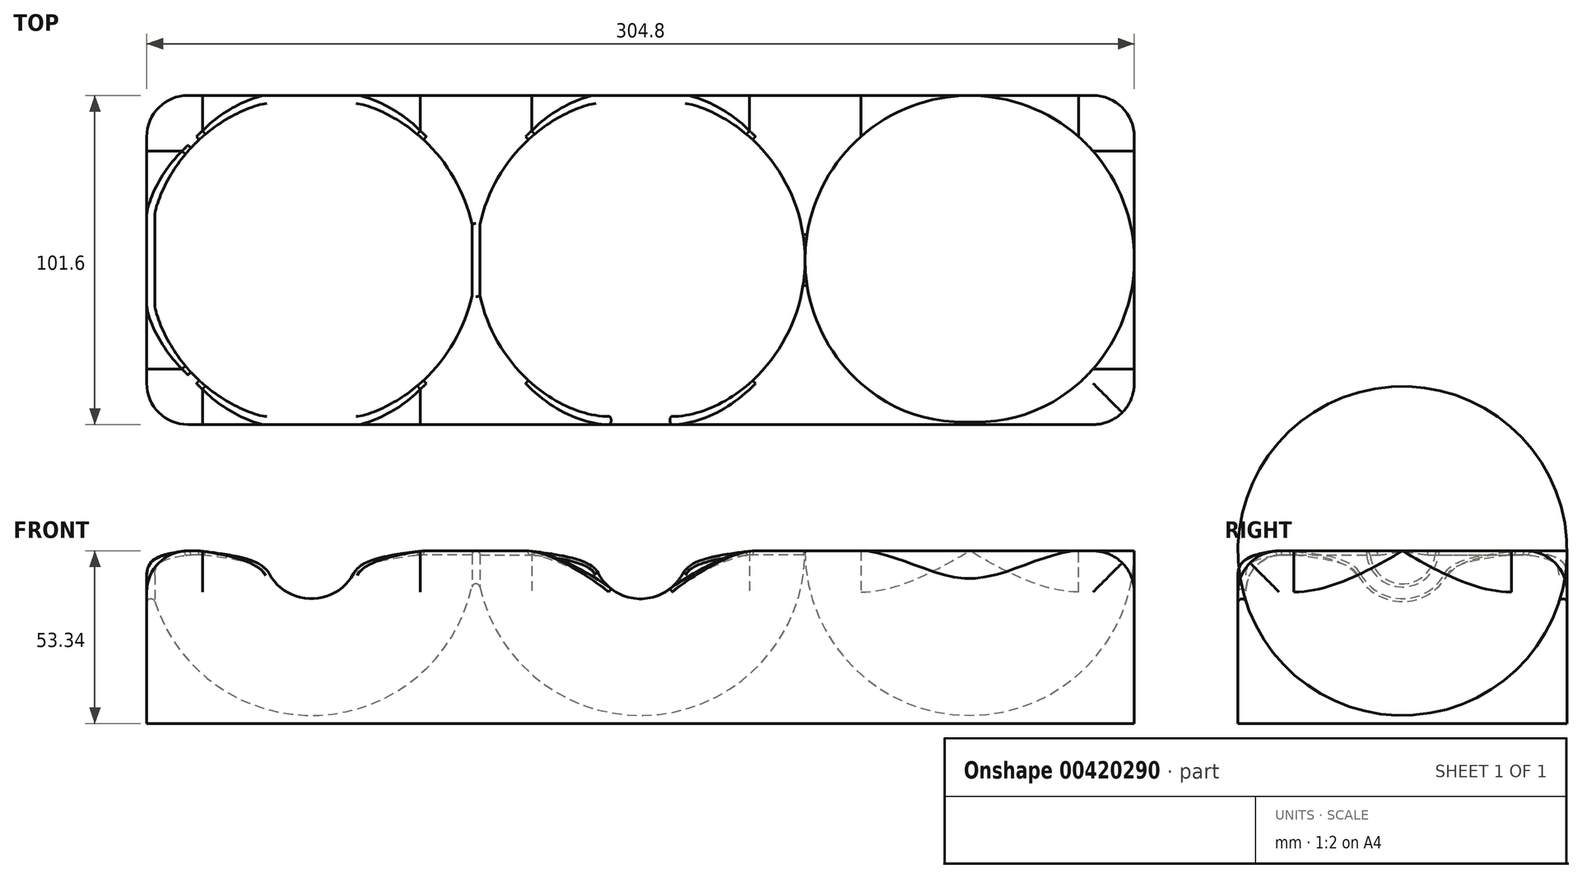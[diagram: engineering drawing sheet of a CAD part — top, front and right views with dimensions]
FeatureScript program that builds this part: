
annotation { "Feature Type Name" : "Feature", "Feature Type Description" : "" }
export const myFeature = defineFeature(function(context is Context, id is Id, definition is map)
    precondition{}
    {
        {
            var Q0;
            Q0=qCreatedBy(makeId("Top.planeOp"),FACE);
            var sketch = newSketch(context, id + "F0", { "sketchPlane" : qUnion([Q0])});
            skLineSegment(sketch, "E0.bottom", {"start": v(-140.38, -23.85) * mm, "end": v(164.42, -23.85) * mm});
            skLineSegment(sketch, "E0.top", {"start": v(-140.38, -125.45) * mm, "end": v(164.42, -125.45) * mm});
            skLineSegment(sketch, "E0.left", {"start": v(-140.38, -23.85) * mm, "end": v(-140.38, -125.45) * mm});
            skLineSegment(sketch, "E0.right", {"start": v(164.42, -23.85) * mm, "end": v(164.42, -125.45) * mm});
            skSolve(sketch);
        }
        {
            var Q0;
            Q0=makeQuery(id+"F0.imprint","IMPRINT",FACE,{"disambiguationData":[TD([[makeQuery(id+"F0.imprint","IMPRINT",EDGE,{"derivedFrom":sQuery(id+"F0.wireOp",EDGE,"E0.bottom")}),-1.0]])]});
            extrude(context, id + "F1", {"entities" : qUnion([Q0]), "depth" : 53.34 * mm});
        }
        {
            var Q0;
            Q0=makeQuery(id+"F1.opExtrude","CAP_FACE",FACE,{"disambiguationData":[OSD([sQuery(id+"F0.wireOp",EDGE,"E0.bottom"),sQuery(id+"F0.wireOp",EDGE,"E0.top"),sQuery(id+"F0.wireOp",EDGE,"E0.left"),sQuery(id+"F0.wireOp",EDGE,"E0.right")])],"isStart":false});
            var sketch = newSketch(context, id + "F2", { "sketchPlane" : qUnion([Q0])});
            skLineSegment(sketch, "E1", {"start": v(-140.38, -23.85) * mm, "end": v(-89.58, -23.85) * mm});
            skLineSegment(sketch, "E2", {"start": v(-89.58, -23.85) * mm, "end": v(-89.58, -125.45) * mm});
            skArc(sketch, "E3", {"start": v(-89.58, -23.85) * mm, "mid": v(-140.38, -74.65) * mm, "end": v(-89.58, -125.45) * mm});
            skArc(sketch, "E4.1.0.0", {"start": v(12.02, -23.85) * mm, "mid": v(-38.78, -74.65) * mm, "end": v(12.02, -125.45) * mm});
            skLineSegment(sketch, "E4.1.0.1", {"start": v(12.02, -23.85) * mm, "end": v(12.02, -125.45) * mm});
            skArc(sketch, "E4.2.0.0", {"start": v(113.62, -23.85) * mm, "mid": v(62.82, -74.65) * mm, "end": v(113.62, -125.45) * mm});
            skLineSegment(sketch, "E4.2.0.1", {"start": v(113.62, -23.85) * mm, "end": v(113.62, -125.45) * mm});
            skLineSegment(sketch, "E4.direction1", {"start": v(-89.58, -125.45) * mm, "end": v(12.02, -125.45) * mm, "construction": true});
            skSolve(sketch);
        }
        {
            var Q0;
            {var subQ0=sQuery(id+"F2.wireOp",EDGE,"E2");Q0=makeQuery(id+"F2.imprint","IMPRINT",FACE,{"disambiguationData":[TD([[makeQuery(id+"F2.imprint","IMPRINT",EDGE,{"derivedFrom":subQ0}),-1.0]])]});}
            var Q1;
            Q1=sQuery(id+"F2.wireOp",EDGE,"E2");
            revolve(context, id + "F3", {"operationType" : NewBodyOperationType.REMOVE, "entities" : qUnion([Q0]), "axis" : qUnion([Q1]), "revolveType" : RevolveType.FULL, "oppositeDirection" : true});
        }
        {
            var Q0;
            Q0=makeQuery(id+"F2.imprint","IMPRINT",FACE,{"disambiguationData":[TD([[makeQuery(id+"F2.imprint","IMPRINT",EDGE,{"derivedFrom":sQuery(id+"F2.wireOp",EDGE,"E4.1.0.0")}),1.0]])]});
            var Q1;
            Q1=sQuery(id+"F2.wireOp",EDGE,"E4.1.0.1");
            revolve(context, id + "F4", {"operationType" : NewBodyOperationType.REMOVE, "entities" : qUnion([Q0]), "axis" : qUnion([Q1]), "revolveType" : RevolveType.FULL, "oppositeDirection" : true});
        }
        {
            var Q0;
            Q0=makeQuery(id+"F2.imprint","IMPRINT",FACE,{"disambiguationData":[TD([[makeQuery(id+"F2.imprint","IMPRINT",EDGE,{"derivedFrom":sQuery(id+"F2.wireOp",EDGE,"E4.2.0.0")}),1.0]])]});
            var Q1;
            Q1=sQuery(id+"F2.wireOp",EDGE,"E4.2.0.1");
            revolve(context, id + "F5", {"operationType" : NewBodyOperationType.REMOVE, "entities" : qUnion([Q0]), "axis" : qUnion([Q1]), "revolveType" : RevolveType.FULL, "oppositeDirection" : true});
        }
        {
            var Q0;
            {var subQ0=sQuery(id+"F0.wireOp",EDGE,"E0.right");var subQ1=sQuery(id+"F0.wireOp",EDGE,"E0.top");var subQ4=makeQuery(id+"F3.opRevolve","SWEPT_FACE",FACE,{"disambiguationData":[OSD([sQuery(id+"F2.wireOp",EDGE,"E3")])]});Q0=makeQuery(id+"F4.boolean.opBoolean","SPLIT",EDGE,{"disambiguationData":[TD([makeQuery(id+"F3.boolean.opBoolean","COPY",FACE,{"derivedFrom":subQ4})])],"derivedFrom":makeQuery(id+"F3.boolean.opBoolean","SPLIT",EDGE,{"disambiguationData":[TD([makeQuery(id+"F1.opExtrude","SWEPT_FACE",FACE,{"disambiguationData":[OSD([subQ0])]})])],"derivedFrom":makeQuery(id+"F1.opExtrude","CAP_EDGE",EDGE,{"disambiguationData":[OSD([subQ1])],"isStart":false})})});}
            var Q1;
            {var subQ0=sQuery(id+"F0.wireOp",EDGE,"E0.left");var subQ1=sQuery(id+"F0.wireOp",EDGE,"E0.top");Q1=makeQuery(id+"F3.boolean.opBoolean","SPLIT",EDGE,{"disambiguationData":[TD([makeQuery(id+"F1.opExtrude","SWEPT_FACE",FACE,{"disambiguationData":[OSD([subQ0])]})])],"derivedFrom":makeQuery(id+"F1.opExtrude","CAP_EDGE",EDGE,{"disambiguationData":[OSD([subQ1])],"isStart":false})});}
            var Q2;
            {var subQ0=sQuery(id+"F0.wireOp",EDGE,"E0.left");var subQ1=sQuery(id+"F0.wireOp",EDGE,"E0.top");Q2=makeQuery(id+"F3.boolean.opBoolean","SPLIT",EDGE,{"disambiguationData":[TD([makeQuery(id+"F1.opExtrude","SWEPT_FACE",FACE,{"disambiguationData":[OSD([subQ1])]})])],"derivedFrom":makeQuery(id+"F1.opExtrude","CAP_EDGE",EDGE,{"disambiguationData":[OSD([subQ0])],"isStart":false})});}
            var Q3;
            {var subQ0=sQuery(id+"F0.wireOp",EDGE,"E0.bottom");var subQ1=sQuery(id+"F0.wireOp",EDGE,"E0.left");Q3=makeQuery(id+"F3.boolean.opBoolean","SPLIT",EDGE,{"disambiguationData":[TD([makeQuery(id+"F1.opExtrude","SWEPT_FACE",FACE,{"disambiguationData":[OSD([subQ0])]})])],"derivedFrom":makeQuery(id+"F1.opExtrude","CAP_EDGE",EDGE,{"disambiguationData":[OSD([subQ1])],"isStart":false})});}
            var Q4;
            {var subQ0=sQuery(id+"F0.wireOp",EDGE,"E0.bottom");var subQ1=sQuery(id+"F0.wireOp",EDGE,"E0.left");Q4=makeQuery(id+"F3.boolean.opBoolean","SPLIT",EDGE,{"disambiguationData":[TD([makeQuery(id+"F1.opExtrude","SWEPT_FACE",FACE,{"disambiguationData":[OSD([subQ1])]})])],"derivedFrom":makeQuery(id+"F1.opExtrude","CAP_EDGE",EDGE,{"disambiguationData":[OSD([subQ0])],"isStart":false})});}
            var Q5;
            {var subQ0=sQuery(id+"F0.wireOp",EDGE,"E0.bottom");var subQ2=sQuery(id+"F0.wireOp",EDGE,"E0.right");var subQ4=makeQuery(id+"F3.opRevolve","SWEPT_FACE",FACE,{"disambiguationData":[OSD([sQuery(id+"F2.wireOp",EDGE,"E3")])]});Q5=makeQuery(id+"F4.boolean.opBoolean","SPLIT",EDGE,{"disambiguationData":[TD([makeQuery(id+"F3.boolean.opBoolean","COPY",FACE,{"derivedFrom":subQ4})])],"derivedFrom":makeQuery(id+"F3.boolean.opBoolean","SPLIT",EDGE,{"disambiguationData":[TD([makeQuery(id+"F1.opExtrude","SWEPT_FACE",FACE,{"disambiguationData":[OSD([subQ2])]})])],"derivedFrom":makeQuery(id+"F1.opExtrude","CAP_EDGE",EDGE,{"disambiguationData":[OSD([subQ0])],"isStart":false})})});}
            var Q6;
            {var subQ0=sQuery(id+"F0.wireOp",EDGE,"E0.bottom");var subQ2=sQuery(id+"F0.wireOp",EDGE,"E0.right");var subQ4=makeQuery(id+"F4.opRevolve","SWEPT_FACE",FACE,{"disambiguationData":[OSD([sQuery(id+"F2.wireOp",EDGE,"E4.1.0.0")])]});var subQ5=makeQuery(id+"F1.opExtrude","SWEPT_FACE",FACE,{"disambiguationData":[OSD([subQ2])]});Q6=makeQuery(id+"F5.boolean.opBoolean","SPLIT",EDGE,{"disambiguationData":[TD([makeQuery(id+"F4.boolean.opBoolean","COPY",FACE,{"derivedFrom":subQ4})])],"derivedFrom":makeQuery(id+"F4.boolean.opBoolean","SPLIT",EDGE,{"disambiguationData":[TD([subQ5])],"derivedFrom":makeQuery(id+"F3.boolean.opBoolean","SPLIT",EDGE,{"disambiguationData":[TD([subQ5])],"derivedFrom":makeQuery(id+"F1.opExtrude","CAP_EDGE",EDGE,{"disambiguationData":[OSD([subQ0])],"isStart":false})})})});}
            var Q7;
            {var subQ0=sQuery(id+"F0.wireOp",EDGE,"E0.bottom");var subQ2=sQuery(id+"F0.wireOp",EDGE,"E0.right");var subQ3=makeQuery(id+"F1.opExtrude","SWEPT_FACE",FACE,{"disambiguationData":[OSD([subQ2])]});Q7=makeQuery(id+"F5.boolean.opBoolean","SPLIT",EDGE,{"disambiguationData":[TD([subQ3])],"derivedFrom":makeQuery(id+"F4.boolean.opBoolean","SPLIT",EDGE,{"disambiguationData":[TD([subQ3])],"derivedFrom":makeQuery(id+"F3.boolean.opBoolean","SPLIT",EDGE,{"disambiguationData":[TD([subQ3])],"derivedFrom":makeQuery(id+"F1.opExtrude","CAP_EDGE",EDGE,{"disambiguationData":[OSD([subQ0])],"isStart":false})})})});}
            var Q8;
            {var subQ0=sQuery(id+"F0.wireOp",EDGE,"E0.bottom");var subQ1=sQuery(id+"F0.wireOp",EDGE,"E0.right");Q8=makeQuery(id+"F5.boolean.opBoolean","SPLIT",EDGE,{"disambiguationData":[TD([makeQuery(id+"F1.opExtrude","SWEPT_FACE",FACE,{"disambiguationData":[OSD([subQ0])]})])],"derivedFrom":makeQuery(id+"F1.opExtrude","CAP_EDGE",EDGE,{"disambiguationData":[OSD([subQ1])],"isStart":false})});}
            var Q9;
            {var subQ0=sQuery(id+"F0.wireOp",EDGE,"E0.right");var subQ1=sQuery(id+"F0.wireOp",EDGE,"E0.top");Q9=makeQuery(id+"F5.boolean.opBoolean","SPLIT",EDGE,{"disambiguationData":[TD([makeQuery(id+"F1.opExtrude","SWEPT_FACE",FACE,{"disambiguationData":[OSD([subQ1])]})])],"derivedFrom":makeQuery(id+"F1.opExtrude","CAP_EDGE",EDGE,{"disambiguationData":[OSD([subQ0])],"isStart":false})});}
            var Q10;
            Q10=makeQuery(id+"F1.opExtrude","SWEPT_EDGE",EDGE,{"disambiguationData":[OSD([sQuery(id+"F0.wireOp",EDGE,"E0.top"),sQuery(id+"F0.wireOp",EDGE,"E0.right")])]});
            var Q11;
            Q11=makeQuery(id+"F1.opExtrude","SWEPT_EDGE",EDGE,{"disambiguationData":[OSD([sQuery(id+"F0.wireOp",EDGE,"E0.bottom"),sQuery(id+"F0.wireOp",EDGE,"E0.right")])]});
            var Q12;
            Q12=makeQuery(id+"F1.opExtrude","SWEPT_EDGE",EDGE,{"disambiguationData":[OSD([sQuery(id+"F0.wireOp",EDGE,"E0.bottom"),sQuery(id+"F0.wireOp",EDGE,"E0.left")])]});
            var Q13;
            Q13=makeQuery(id+"F1.opExtrude","SWEPT_EDGE",EDGE,{"disambiguationData":[OSD([sQuery(id+"F0.wireOp",EDGE,"E0.top"),sQuery(id+"F0.wireOp",EDGE,"E0.left")])]});
            fillet(context, id + "F6", {"entities" : qUnion([Q0, Q1, Q2, Q3, Q4, Q5, Q6, Q7, Q8, Q9, Q10, Q11, Q12, Q13]), "radius" : 12.7 * mm, "tangentPropagation" : true, "allowEdgeOverflow" : false});
        }
        {
            var Q0;
            {var subQ0=makeQuery(id+"F3.opRevolve","SWEPT_FACE",FACE,{"disambiguationData":[OSD([sQuery(id+"F2.wireOp",EDGE,"E3")])]});var subQ1=sQuery(id+"F0.wireOp",EDGE,"E0.bottom");var subQ2=sQuery(id+"F0.wireOp",EDGE,"E0.left");Q0=makeQuery(id+"F6.opFillet","BLEND_EDGE",EDGE,{"blendedFrom":[makeQuery(id+"F3.boolean.opBoolean","SPLIT",EDGE,{"disambiguationData":[TD([makeQuery(id+"F1.opExtrude","SWEPT_FACE",FACE,{"disambiguationData":[OSD([subQ1])]})])],"derivedFrom":makeQuery(id+"F1.opExtrude","CAP_EDGE",EDGE,{"disambiguationData":[OSD([subQ2])],"isStart":false})}),makeQuery(id+"F3.boolean.opBoolean","COPY",FACE,{"derivedFrom":subQ0})],"blendedInto":[makeQuery(id+"F3.boolean.opBoolean","COPY",FACE,{"derivedFrom":subQ0})]});}
            var Q1;
            {var subQ0=makeQuery(id+"F4.opRevolve","SWEPT_FACE",FACE,{"disambiguationData":[OSD([sQuery(id+"F2.wireOp",EDGE,"E4.1.0.0")])]});var subQ1=makeQuery(id+"F4.boolean.opBoolean","COPY",FACE,{"derivedFrom":subQ0});var subQ2=sQuery(id+"F0.wireOp",EDGE,"E0.right");var subQ3=sQuery(id+"F0.wireOp",EDGE,"E0.top");var subQ6=makeQuery(id+"F1.opExtrude","SWEPT_FACE",FACE,{"disambiguationData":[OSD([subQ2])]});Q1=makeQuery(id+"F6.opFillet","BLEND_EDGE",EDGE,{"blendedFrom":[makeQuery(id+"F5.boolean.opBoolean","SPLIT",EDGE,{"disambiguationData":[TD([subQ1])],"derivedFrom":makeQuery(id+"F4.boolean.opBoolean","SPLIT",EDGE,{"disambiguationData":[TD([subQ6])],"derivedFrom":makeQuery(id+"F3.boolean.opBoolean","SPLIT",EDGE,{"disambiguationData":[TD([subQ6])],"derivedFrom":makeQuery(id+"F1.opExtrude","CAP_EDGE",EDGE,{"disambiguationData":[OSD([subQ3])],"isStart":false})})})}),subQ1],"blendedInto":[subQ1]});}
            var Q2;
            {var subQ0=sQuery(id+"F0.wireOp",EDGE,"E0.right");var subQ1=sQuery(id+"F0.wireOp",EDGE,"E0.top");var subQ2=sQuery(id+"F0.wireOp",EDGE,"E0.bottom");var subQ3=makeQuery(id+"F1.opExtrude","CAP_FACE",FACE,{"disambiguationData":[OSD([subQ2,subQ1,sQuery(id+"F0.wireOp",EDGE,"E0.left"),subQ0])],"isStart":false});var subQ4=makeQuery(id+"F1.opExtrude","SWEPT_FACE",FACE,{"disambiguationData":[OSD([subQ1])]});var subQ5=makeQuery(id+"F4.opRevolve","SWEPT_FACE",FACE,{"disambiguationData":[OSD([sQuery(id+"F2.wireOp",EDGE,"E4.1.0.0")])]});Q2=makeQuery(id+"F5.boolean.opBoolean","SPLIT",EDGE,{"disambiguationData":[TD([subQ4])],"derivedFrom":makeQuery(id+"F4.boolean.opBoolean","INTERSECT",EDGE,{"disambiguationData":[OD(0.0)],"derivedFrom":[makeQuery(id+"F3.boolean.opBoolean","SPLIT",FACE,{"disambiguationData":[TD([makeQuery(id+"F1.opExtrude","SWEPT_FACE",FACE,{"disambiguationData":[OSD([subQ2])]}),subQ3,subQ4,makeQuery(id+"F1.opExtrude","SWEPT_FACE",FACE,{"disambiguationData":[OSD([subQ0])]}),makeQuery(id+"F3.opRevolve","SWEPT_FACE",FACE,{"disambiguationData":[OSD([sQuery(id+"F2.wireOp",EDGE,"E3")])]})])],"derivedFrom":subQ3}),subQ5]})});}
            var Q3;
            {var subQ0=sQuery(id+"F0.wireOp",EDGE,"E0.bottom");var subQ1=makeQuery(id+"F1.opExtrude","SWEPT_FACE",FACE,{"disambiguationData":[OSD([subQ0])]});var subQ2=sQuery(id+"F0.wireOp",EDGE,"E0.right");var subQ3=sQuery(id+"F0.wireOp",EDGE,"E0.top");var subQ4=makeQuery(id+"F1.opExtrude","CAP_FACE",FACE,{"disambiguationData":[OSD([subQ0,subQ3,sQuery(id+"F0.wireOp",EDGE,"E0.left"),subQ2])],"isStart":false});var subQ5=makeQuery(id+"F4.opRevolve","SWEPT_FACE",FACE,{"disambiguationData":[OSD([sQuery(id+"F2.wireOp",EDGE,"E4.1.0.0")])]});Q3=makeQuery(id+"F5.boolean.opBoolean","SPLIT",EDGE,{"disambiguationData":[TD([subQ1])],"derivedFrom":makeQuery(id+"F4.boolean.opBoolean","INTERSECT",EDGE,{"disambiguationData":[OD(0.0)],"derivedFrom":[makeQuery(id+"F3.boolean.opBoolean","SPLIT",FACE,{"disambiguationData":[TD([subQ1,subQ4,makeQuery(id+"F1.opExtrude","SWEPT_FACE",FACE,{"disambiguationData":[OSD([subQ3])]}),makeQuery(id+"F1.opExtrude","SWEPT_FACE",FACE,{"disambiguationData":[OSD([subQ2])]}),makeQuery(id+"F3.opRevolve","SWEPT_FACE",FACE,{"disambiguationData":[OSD([sQuery(id+"F2.wireOp",EDGE,"E3")])]})])],"derivedFrom":subQ4}),subQ5]})});}
            var Q4;
            {var subQ0=makeQuery(id+"F5.opRevolve","SWEPT_FACE",FACE,{"disambiguationData":[OSD([sQuery(id+"F2.wireOp",EDGE,"E4.2.0.0")])]});var subQ1=sQuery(id+"F0.wireOp",EDGE,"E0.right");var subQ2=sQuery(id+"F0.wireOp",EDGE,"E0.top");var subQ5=makeQuery(id+"F1.opExtrude","SWEPT_FACE",FACE,{"disambiguationData":[OSD([subQ1])]});Q4=makeQuery(id+"F6.opFillet","BLEND_EDGE",EDGE,{"blendedFrom":[makeQuery(id+"F5.boolean.opBoolean","SPLIT",EDGE,{"disambiguationData":[TD([subQ5])],"derivedFrom":makeQuery(id+"F4.boolean.opBoolean","SPLIT",EDGE,{"disambiguationData":[TD([subQ5])],"derivedFrom":makeQuery(id+"F3.boolean.opBoolean","SPLIT",EDGE,{"disambiguationData":[TD([subQ5])],"derivedFrom":makeQuery(id+"F1.opExtrude","CAP_EDGE",EDGE,{"disambiguationData":[OSD([subQ2])],"isStart":false})})})}),makeQuery(id+"F5.boolean.opBoolean","COPY",FACE,{"derivedFrom":subQ0})],"blendedInto":[makeQuery(id+"F5.boolean.opBoolean","COPY",FACE,{"derivedFrom":subQ0})]});}
            fillet(context, id + "F7", {"entities" : qUnion([Q0, Q1, Q2, Q3, Q4]), "radius" : 1.27 * mm, "tangentPropagation" : true, "allowEdgeOverflow" : false});
        }
    });
